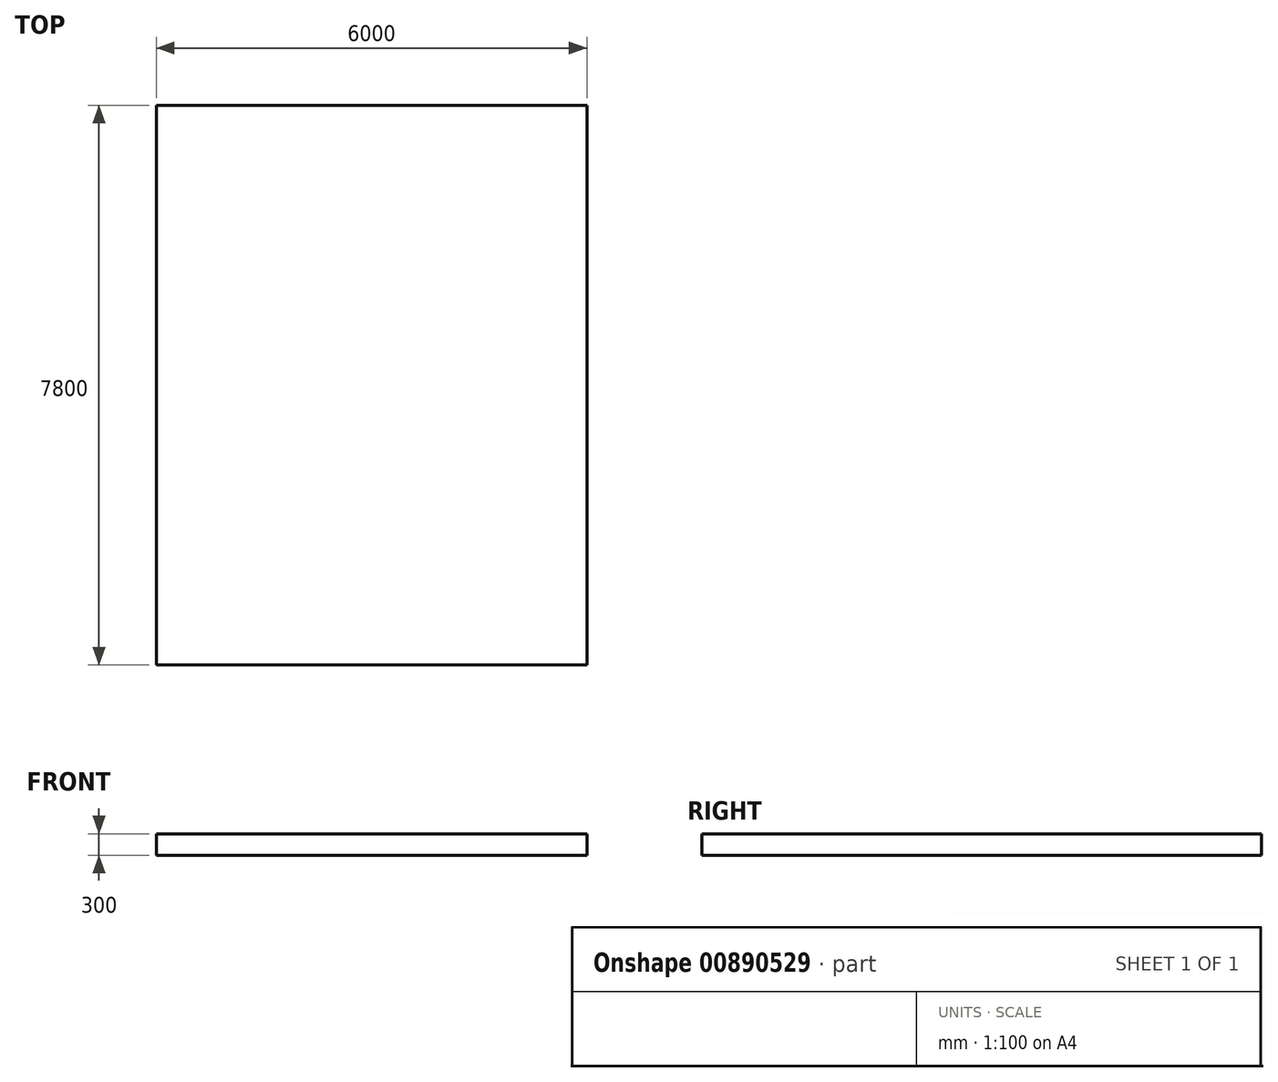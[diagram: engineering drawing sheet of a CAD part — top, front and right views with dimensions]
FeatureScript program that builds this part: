
annotation { "Feature Type Name" : "Feature", "Feature Type Description" : "" }
export const myFeature = defineFeature(function(context is Context, id is Id, definition is map)
    precondition{}
    {
        {
            var Q0;
            Q0=qCreatedBy(makeId("Top.planeOp"),FACE);
            var sketch = newSketch(context, id + "F0", { "sketchPlane" : qUnion([Q0])});
            skLineSegment(sketch, "E0.bottom", {"start": v(3000, -3900) * mm, "end": v(-3000, -3900) * mm});
            skLineSegment(sketch, "E0.top", {"start": v(3000, 3900) * mm, "end": v(-3000, 3900) * mm});
            skLineSegment(sketch, "E0.left", {"start": v(3000, -3900) * mm, "end": v(3000, 3900) * mm});
            skLineSegment(sketch, "E0.right", {"start": v(-3000, -3900) * mm, "end": v(-3000, 3900) * mm});
            skPoint(sketch, "E0.middle", {"position": v(0, 0) * mm});
            skSolve(sketch);
        }
        {
            var Q0;
            Q0=makeQuery(id+"F0.imprint","IMPRINT",FACE,{"disambiguationData":[TD([[makeQuery(id+"F0.imprint","IMPRINT",EDGE,{"derivedFrom":sQuery(id+"F0.wireOp",EDGE,"E0.bottom")}),-1.0]])]});
            extrude(context, id + "F1", {"entities" : qUnion([Q0]), "depth" : 300 * mm, "offsetDistance" : 25 * mm});
        }
    });
